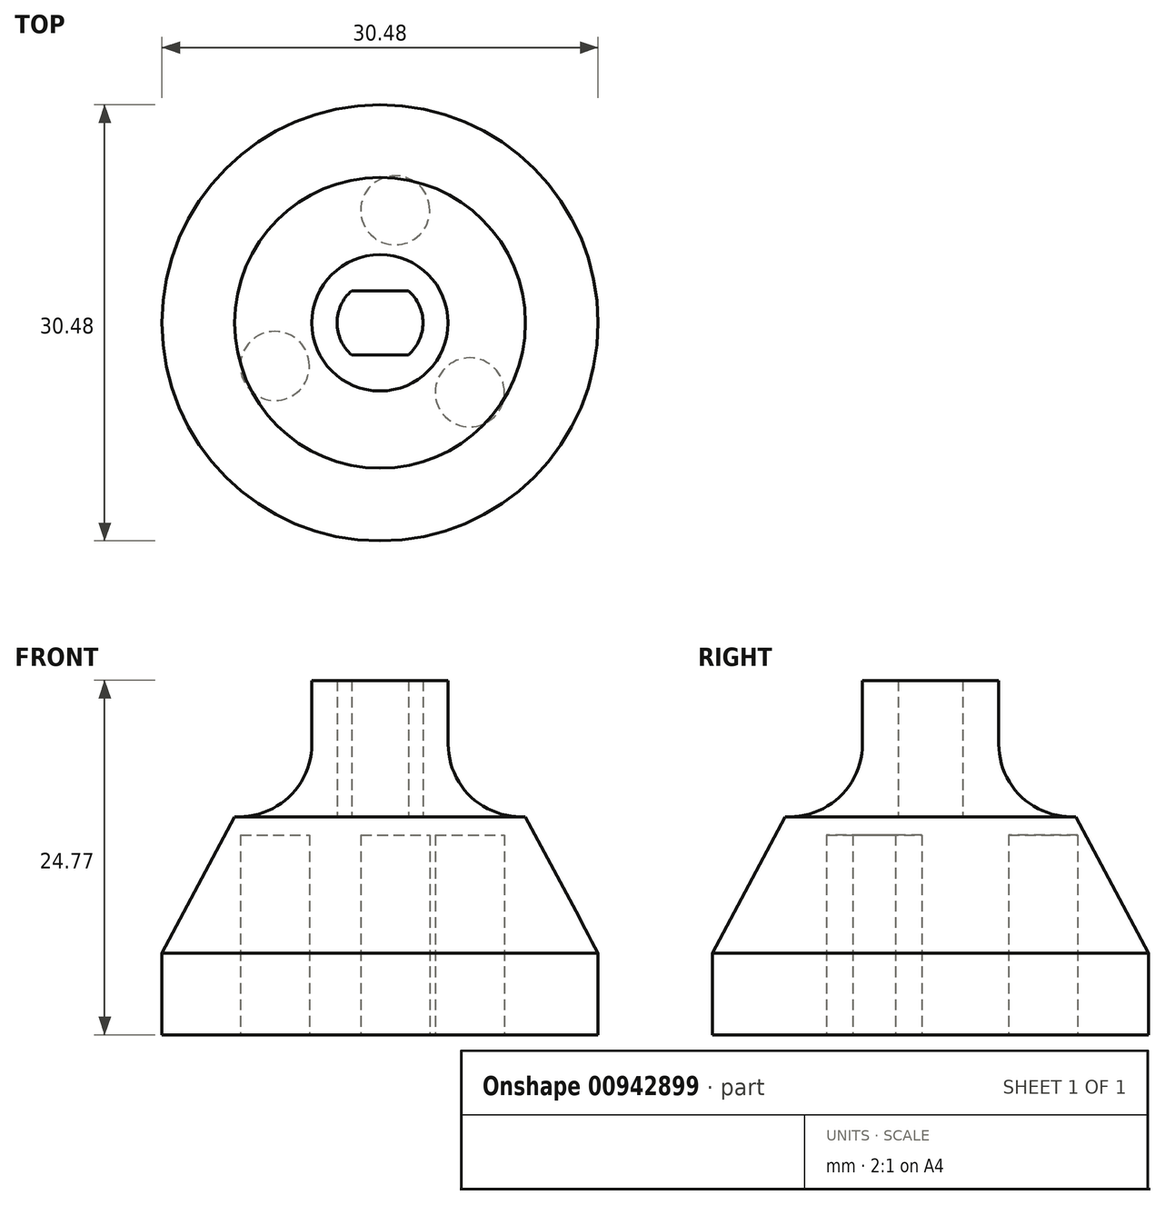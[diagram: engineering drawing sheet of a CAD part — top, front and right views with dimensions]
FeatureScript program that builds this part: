
annotation { "Feature Type Name" : "Feature", "Feature Type Description" : "" }
export const myFeature = defineFeature(function(context is Context, id is Id, definition is map)
    precondition{}
    {
        {
            var Q0;
            Q0=qCreatedBy(makeId("Top.planeOp"),FACE);
            var sketch = newSketch(context, id + "F0", { "sketchPlane" : qUnion([Q0])});
            skCircle(sketch, "E0", {"center": v(0, 0) * mm, "radius": 4.76 * mm});
            skSolve(sketch);
        }
        {
            var Q0;
            Q0=qSketchRegion(id+"F0",true);
            extrude(context, id + "F1", {"entities" : qUnion([Q0]), "depth" : 9.52 * mm, "offsetDistance" : 25.4 * mm, "hasSecondDirection" : true, "secondDirectionOppositeDirection" : true, "secondDirectionDepth" : 6.35 * mm});
        }
        {
            var Q0;
            Q0=qCreatedBy(makeId("Top.planeOp"),FACE);
            var sketch = newSketch(context, id + "F2", { "sketchPlane" : qUnion([Q0])});
            skCircle(sketch, "E1", {"center": v(0, 0) * mm, "radius": 3 * mm});
            skLineSegment(sketch, "E2", {"start": v(-1.98, 2.25) * mm, "end": v(1.98, 2.25) * mm});
            skLineSegment(sketch, "E3", {"start": v(-1.98, -2.25) * mm, "end": v(1.98, -2.25) * mm});
            skSolve(sketch);
        }
        {
            var Q0;
            {var subQ0=sQuery(id+"F2.wireOp",EDGE,"E2");Q0=makeQuery(id+"F2.imprint","IMPRINT",FACE,{"disambiguationData":[TD([[makeQuery(id+"F2.imprint","IMPRINT",EDGE,{"derivedFrom":subQ0}),-1.0]])]});}
            extrude(context, id + "F3", {"entities" : qUnion([Q0]), "operationType" : NewBodyOperationType.REMOVE, "endBound" : BoundingType.THROUGH_ALL, "depth" : 25.4 * mm, "offsetDistance" : 25.4 * mm});
        }
        {
            var Q0;
            Q0=qCreatedBy(makeId("Top.planeOp"),FACE);
            var sketch = newSketch(context, id + "F4", { "sketchPlane" : qUnion([Q0])});
            skCircle(sketch, "E4", {"center": v(0, 0) * mm, "radius": 15.24 * mm});
            skSolve(sketch);
        }
        {
            var Q0;
            Q0 = qSketchRegion(id + "F4", true);
            var Q1;
            Q1=sQuery(id+"F4.wireOp",EDGE,"E4");
            extrude(context, id + "F5", {"entities" : qUnion([Q0]), "operationType" : NewBodyOperationType.ADD, "surfaceEntities" : qUnion([Q1]), "oppositeDirection" : true, "depth" : 15.24 * mm, "offsetDistance" : 25.4 * mm});
        }
        {
            var Q0;
            Q0=makeQuery(id+"F5.opExtrude","CAP_FACE",FACE,{"disambiguationData":[OSD([sQuery(id+"F4.wireOp",EDGE,"E4")])],"isStart":false});
            var sketch = newSketch(context, id + "F6", { "sketchPlane" : qUnion([Q0])});
            skCircle(sketch, "E5", {"center": v(6.28, 4.86) * mm, "radius": 2.41 * mm});
            skCircle(sketch, "E6", {"center": v(0, 0) * mm, "radius": 7.94 * mm, "construction": true});
            skCircle(sketch, "E7", {"center": v(-7.35, 3) * mm, "radius": 2.41 * mm});
            skLineSegment(sketch, "E8", {"start": v(6.28, 4.86) * mm, "end": v(-7.35, 3) * mm, "construction": true});
            skLineSegment(sketch, "E9", {"start": v(-7.35, 3) * mm, "end": v(1.07, -7.87) * mm, "construction": true});
            skLineSegment(sketch, "E10", {"start": v(1.07, -7.87) * mm, "end": v(6.28, 4.86) * mm, "construction": true});
            skCircle(sketch, "E11", {"center": v(1.07, -7.87) * mm, "radius": 2.41 * mm});
            skSolve(sketch);
        }
        {
            var Q0;
            Q0=makeQuery(id+"F6.imprint","IMPRINT",FACE,{"disambiguationData":[TD([[makeQuery(id+"F6.imprint","IMPRINT",EDGE,{"derivedFrom":sQuery(id+"F6.wireOp",EDGE,"E11")}),1.0]])]});
            var Q1;
            Q1=makeQuery(id+"F6.imprint","IMPRINT",FACE,{"disambiguationData":[TD([[makeQuery(id+"F6.imprint","IMPRINT",EDGE,{"derivedFrom":sQuery(id+"F6.wireOp",EDGE,"E5")}),1.0]])]});
            var Q2;
            Q2=makeQuery(id+"F6.imprint","IMPRINT",FACE,{"disambiguationData":[TD([[makeQuery(id+"F6.imprint","IMPRINT",EDGE,{"derivedFrom":sQuery(id+"F6.wireOp",EDGE,"E7")}),1.0]])]});
            extrude(context, id + "F7", {"entities" : qUnion([Q0, Q1, Q2]), "operationType" : NewBodyOperationType.REMOVE, "oppositeDirection" : true, "depth" : 13.97 * mm, "offsetDistance" : 25.4 * mm});
        }
        {
            var Q0;
            Q0=makeQuery(id+"F5.opExtrude","CAP_EDGE",EDGE,{"disambiguationData":[OSD([sQuery(id+"F4.wireOp",EDGE,"E4")])],"isStart":true});
            chamfer(context, id + "F8", {"entities" : qUnion([Q0]), "chamferType" : ChamferType.TWO_OFFSETS, "width1" : 5.08 * mm, "oppositeDirection" : false, "width2" : 9.52 * mm, "tangentPropagation" : true});
        }
        {
            var Q0;
            Q0=makeQuery(id+"F5.boolean.opBoolean","INTERSECT",EDGE,{"derivedFrom":[makeQuery(id+"F1.opExtrude","SWEPT_FACE",FACE,{"disambiguationData":[OSD([sQuery(id+"F0.wireOp",EDGE,"E0")])]}),makeQuery(id+"F5.opExtrude","CAP_FACE",FACE,{"disambiguationData":[OSD([sQuery(id+"F4.wireOp",EDGE,"E4")])],"isStart":true})]});
            fillet(context, id + "F9", {"entities" : qUnion([Q0]), "radius" : 5.08 * mm, "tangentPropagation" : true, "allowEdgeOverflow" : false});
        }
    });
